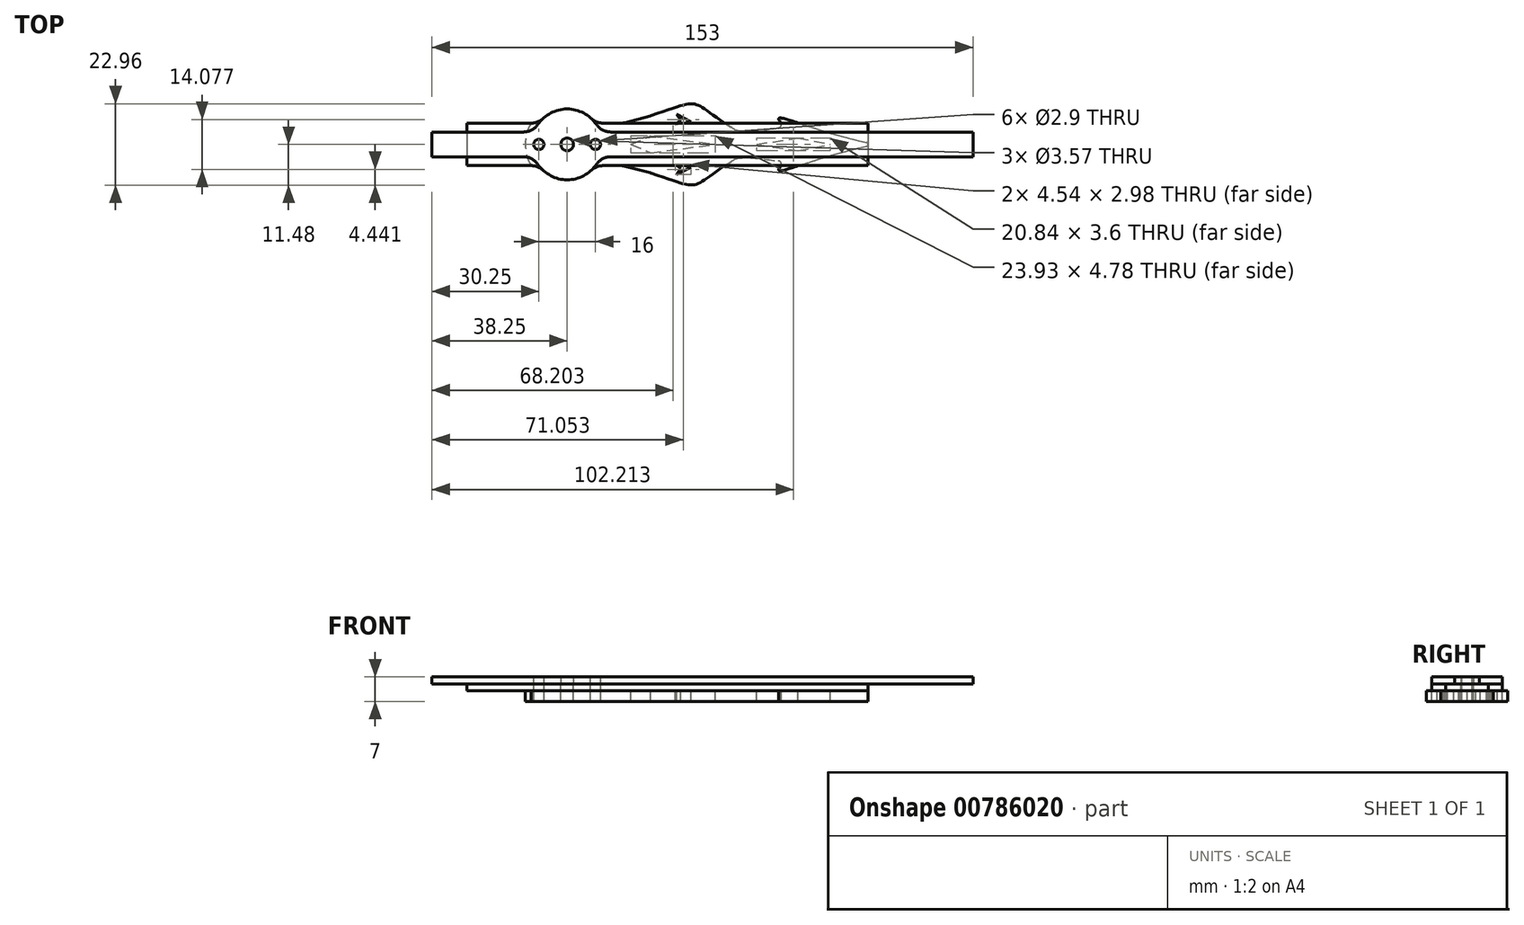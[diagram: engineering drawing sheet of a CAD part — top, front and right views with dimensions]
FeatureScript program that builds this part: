
annotation { "Feature Type Name" : "Feature", "Feature Type Description" : "" }
export const myFeature = defineFeature(function(context is Context, id is Id, definition is map)
    precondition{}
    {
        {
            var Q0;
            Q0=qCreatedBy(makeId("Top.planeOp"),FACE);
            var sketch = newSketch(context, id + "F0", { "sketchPlane" : qUnion([Q0])});
            skCircle(sketch, "E0", {"center": v(0, 0) * mm, "radius": 1.79 * mm});
            skLineSegment(sketch, "E1.bottom", {"start": v(-38.25, 3.5) * mm, "end": v(114.75, 3.5) * mm});
            skLineSegment(sketch, "E1.top", {"start": v(-38.25, -3.5) * mm, "end": v(114.75, -3.5) * mm});
            skLineSegment(sketch, "E1.left", {"start": v(-38.25, 3.5) * mm, "end": v(-38.25, -3.5) * mm});
            skLineSegment(sketch, "E1.right", {"start": v(114.75, 3.5) * mm, "end": v(114.75, -3.5) * mm});
            skCircle(sketch, "E2", {"center": v(0, 0) * mm, "radius": 10 * mm});
            skSolve(sketch);
        }
        {
            var Q0;
            Q0=qSketchRegion(id+"F0",true);
            extrude(context, id + "F1", {"entities" : qUnion([Q0]), "depth" : 2 * mm});
        }
        {
            var Q0;
            Q0=qCreatedBy(makeId("Top.planeOp"),FACE);
            var sketch = newSketch(context, id + "F2", { "sketchPlane" : qUnion([Q0])});
            skCircle(sketch, "E3", {"center": v(0, 0) * mm, "radius": 1.79 * mm});
            skLineSegment(sketch, "E4.bottom", {"start": v(-28.33, 6) * mm, "end": v(85, 6) * mm});
            skLineSegment(sketch, "E4.top", {"start": v(-28.33, -6) * mm, "end": v(85, -6) * mm});
            skLineSegment(sketch, "E4.left", {"start": v(-28.33, 6) * mm, "end": v(-28.33, -6) * mm});
            skLineSegment(sketch, "E4.right", {"start": v(85, 6) * mm, "end": v(85, -6) * mm});
            skCircle(sketch, "E5", {"center": v(0, 0) * mm, "radius": 10 * mm});
            skSolve(sketch);
        }
        {
            var Q0;
            Q0=qSketchRegion(id+"F2",true);
            extrude(context, id + "F3", {"entities" : qUnion([Q0]), "oppositeDirection" : true, "depth" : 2 * mm});
        }
        {
            var Q0;
            Q0=makeQuery(id+"F1.opExtrude","CAP_FACE",FACE,{"disambiguationData":[OSD([sQuery(id+"F0.wireOp",EDGE,"E0"),sQuery(id+"F0.wireOp",EDGE,"E1.bottom"),sQuery(id+"F0.wireOp",EDGE,"E1.top"),sQuery(id+"F0.wireOp",EDGE,"E1.left"),sQuery(id+"F0.wireOp",EDGE,"E1.right"),sQuery(id+"F0.wireOp",EDGE,"E2")])],"isStart":false});
            var sketch = newSketch(context, id + "F4", { "sketchPlane" : qUnion([Q0])});
            skCircle(sketch, "E6", {"center": v(8, 0) * mm, "radius": 1.45 * mm});
            skLineSegment(sketch, "E7", {"start": v(0, 0) * mm, "end": v(16, 0) * mm, "construction": true});
            skLineSegment(sketch, "E8", {"start": v(0, 0) * mm, "end": v(0, 19.04) * mm, "construction": true});
            skCircle(sketch, "E9.MirrorC", {"center": v(-8, 0) * mm, "radius": 1.45 * mm});
            skSolve(sketch);
        }
        {
            var Q0;
            Q0=qSketchRegion(id+"F4",true);
            extrude(context, id + "F5", {"entities" : qUnion([Q0]), "operationType" : NewBodyOperationType.REMOVE, "oppositeDirection" : true, "depth" : 25 * mm, "offsetDistance" : 25 * mm});
        }
        {
            var Q0;
            {var subQ0=sQuery(id+"F0.wireOp",EDGE,"E2");var subQ1=sQuery(id+"F0.wireOp",EDGE,"E1.top");Q0=makeQuery(id+"F1.opExtrude","SWEPT_EDGE",EDGE,{"disambiguationData":[OSD([subQ1,subQ0]),TDD([makeQuery(id+"F0.imprint","INTERSECT",VERTEX,{"disambiguationData":[OD(1.0)],"derivedFrom":[subQ1,subQ0]})])]});}
            var Q1;
            {var subQ0=sQuery(id+"F0.wireOp",EDGE,"E2");var subQ1=sQuery(id+"F0.wireOp",EDGE,"E1.bottom");Q1=makeQuery(id+"F1.opExtrude","SWEPT_EDGE",EDGE,{"disambiguationData":[OSD([subQ1,subQ0]),TDD([makeQuery(id+"F0.imprint","INTERSECT",VERTEX,{"disambiguationData":[OD(1.0)],"derivedFrom":[subQ1,subQ0]})])]});}
            var Q2;
            {var subQ0=sQuery(id+"F0.wireOp",EDGE,"E2");var subQ1=sQuery(id+"F0.wireOp",EDGE,"E1.bottom");Q2=makeQuery(id+"F1.opExtrude","SWEPT_EDGE",EDGE,{"disambiguationData":[OSD([subQ1,subQ0]),TDD([makeQuery(id+"F0.imprint","INTERSECT",VERTEX,{"disambiguationData":[OD(0.0)],"derivedFrom":[subQ1,subQ0]})])]});}
            var Q3;
            {var subQ0=sQuery(id+"F0.wireOp",EDGE,"E2");var subQ1=sQuery(id+"F0.wireOp",EDGE,"E1.top");Q3=makeQuery(id+"F1.opExtrude","SWEPT_EDGE",EDGE,{"disambiguationData":[OSD([subQ1,subQ0]),TDD([makeQuery(id+"F0.imprint","INTERSECT",VERTEX,{"disambiguationData":[OD(0.0)],"derivedFrom":[subQ1,subQ0]})])]});}
            var Q4;
            {var subQ0=sQuery(id+"F2.wireOp",EDGE,"E5");var subQ1=sQuery(id+"F2.wireOp",EDGE,"E4.top");Q4=makeQuery(id+"F3.opExtrude","SWEPT_EDGE",EDGE,{"disambiguationData":[OSD([subQ1,subQ0]),TDD([makeQuery(id+"F2.imprint","INTERSECT",VERTEX,{"disambiguationData":[OD(0.0)],"derivedFrom":[subQ1,subQ0]})])]});}
            var Q5;
            {var subQ0=sQuery(id+"F2.wireOp",EDGE,"E5");var subQ1=sQuery(id+"F2.wireOp",EDGE,"E4.bottom");Q5=makeQuery(id+"F3.opExtrude","SWEPT_EDGE",EDGE,{"disambiguationData":[OSD([subQ1,subQ0]),TDD([makeQuery(id+"F2.imprint","INTERSECT",VERTEX,{"disambiguationData":[OD(1.0)],"derivedFrom":[subQ1,subQ0]})])]});}
            var Q6;
            {var subQ0=sQuery(id+"F2.wireOp",EDGE,"E5");var subQ1=sQuery(id+"F2.wireOp",EDGE,"E4.top");Q6=makeQuery(id+"F3.opExtrude","SWEPT_EDGE",EDGE,{"disambiguationData":[OSD([subQ1,subQ0]),TDD([makeQuery(id+"F2.imprint","INTERSECT",VERTEX,{"disambiguationData":[OD(1.0)],"derivedFrom":[subQ1,subQ0]})])]});}
            var Q7;
            {var subQ0=sQuery(id+"F2.wireOp",EDGE,"E5");var subQ1=sQuery(id+"F2.wireOp",EDGE,"E4.bottom");Q7=makeQuery(id+"F3.opExtrude","SWEPT_EDGE",EDGE,{"disambiguationData":[OSD([subQ1,subQ0]),TDD([makeQuery(id+"F2.imprint","INTERSECT",VERTEX,{"disambiguationData":[OD(0.0)],"derivedFrom":[subQ1,subQ0]})])]});}
            fillet(context, id + "F6", {"entities" : qUnion([Q0, Q1, Q2, Q3, Q4, Q5, Q6, Q7]), "radius" : 5 * mm, "tangentPropagation" : true, "allowEdgeOverflow" : false});
        }
        {
            var Q0;
            Q0=makeQuery(id+"F3.opExtrude","CAP_FACE",FACE,{"disambiguationData":[OSD([sQuery(id+"F2.wireOp",EDGE,"E3"),sQuery(id+"F2.wireOp",EDGE,"E4.bottom"),sQuery(id+"F2.wireOp",EDGE,"E4.top"),sQuery(id+"F2.wireOp",EDGE,"E4.left"),sQuery(id+"F2.wireOp",EDGE,"E4.right"),sQuery(id+"F2.wireOp",EDGE,"E5")])],"isStart":false});
            var sketch = newSketch(context, id + "F7", { "sketchPlane" : qUnion([Q0])});
            skLineSegment(sketch, "E10", {"start": v(17.99, 0) * mm, "end": v(23.59, 2.39) * mm});
            skLineSegment(sketch, "E11", {"start": v(23.59, 2.39) * mm, "end": v(41.92, 0) * mm});
            skLineSegment(sketch, "E12", {"start": v(53.54, 0) * mm, "end": v(65.27, 1.8) * mm});
            skLineSegment(sketch, "E13", {"start": v(65.27, 1.8) * mm, "end": v(74.38, 0) * mm});
            skLineSegment(sketch, "E14", {"start": v(0, 0) * mm, "end": v(74.38, 0) * mm, "construction": true});
            skCircle(sketch, "E15", {"center": v(0, 0) * mm, "radius": 11.83 * mm});
            skLineSegment(sketch, "E16.bottom", {"start": v(-10.2, 6) * mm, "end": v(-28.33, 6) * mm});
            skLineSegment(sketch, "E16.top", {"start": v(-10.2, -6) * mm, "end": v(-28.33, -6) * mm});
            skLineSegment(sketch, "E16.left", {"start": v(-10.2, 6) * mm, "end": v(-10.2, -6) * mm});
            skLineSegment(sketch, "E16.right", {"start": v(-28.33, 6) * mm, "end": v(-28.33, -6) * mm});
            skCircle(sketch, "E17", {"center": v(0, 0) * mm, "radius": 1.79 * mm});
            skCircle(sketch, "E18", {"center": v(8, 0) * mm, "radius": 1.45 * mm});
            skCircle(sketch, "E19", {"center": v(-8, 0) * mm, "radius": 1.45 * mm});
            skLineSegment(sketch, "E20", {"start": v(15.74, 6) * mm, "end": v(23.59, 8.08) * mm});
            skLineSegment(sketch, "E21", {"start": v(23.59, 8.08) * mm, "end": v(46.56, 4.73) * mm, "construction": true});
            skLineSegment(sketch, "E22", {"start": v(46.56, 4.73) * mm, "end": v(61.74, 4.73) * mm});
            skLineSegment(sketch, "E23", {"start": v(61.74, 4.73) * mm, "end": v(65.27, 4.73) * mm});
            skLineSegment(sketch, "E24", {"start": v(68.44, 6) * mm, "end": v(86.86, 0) * mm});
            skLineSegment(sketch, "E25", {"start": v(15.74, 6) * mm, "end": v(10.2, 6) * mm});
            skLineSegment(sketch, "E26", {"start": v(11.83, 0) * mm, "end": v(17.99, 0) * mm});
            skLineSegment(sketch, "E27", {"start": v(41.92, 0) * mm, "end": v(53.54, 0) * mm});
            skLineSegment(sketch, "E28.MirrorCS", {"start": v(23.59, -2.39) * mm, "end": v(41.92, 0) * mm});
            skLineSegment(sketch, "E29.MirrorCS", {"start": v(17.99, 0) * mm, "end": v(23.59, -2.39) * mm});
            skLineSegment(sketch, "E30.MirrorCS", {"start": v(15.74, -6) * mm, "end": v(23.59, -8.08) * mm});
            skLineSegment(sketch, "E31.MirrorCS", {"start": v(23.59, -8.08) * mm, "end": v(46.56, -4.73) * mm, "construction": true});
            skLineSegment(sketch, "E32.MirrorCS", {"start": v(46.56, -4.73) * mm, "end": v(61.74, -4.73) * mm});
            skLineSegment(sketch, "E33.MirrorCS", {"start": v(61.74, -4.73) * mm, "end": v(65.27, -4.73) * mm, "construction": true});
            skLineSegment(sketch, "E34.MirrorCS", {"start": v(68.44, -6) * mm, "end": v(86.86, 0) * mm});
            skLineSegment(sketch, "E35.MirrorCS", {"start": v(53.54, 0) * mm, "end": v(65.27, -1.8) * mm});
            skLineSegment(sketch, "E36.MirrorCS", {"start": v(65.27, -1.8) * mm, "end": v(74.38, 0) * mm});
            skLineSegment(sketch, "E37.MirrorCS", {"start": v(15.74, -6) * mm, "end": v(10.2, -6) * mm});
            skLineSegment(sketch, "E38", {"start": v(23.59, 8.08) * mm, "end": v(23.59, -8.08) * mm, "construction": true});
            skLineSegment(sketch, "E39", {"start": v(65.27, 4.73) * mm, "end": v(65.27, -4.73) * mm, "construction": true});
            skFitSpline(sketch, "E40", {"points": [v(23.59, 8.08) * mm, v(46.56, 4.73) * mm], "startDerivative": vector(46.65, 15.55) * mm, "endDerivative": vector(38.51, -24.21) * mm});
            skFitSpline(sketch, "E41.MirrorCS", {"points": [v(23.59, -8.08) * mm, v(46.56, -4.73) * mm], "startDerivative": vector(46.65, -15.55) * mm, "endDerivative": vector(38.51, 24.21) * mm});
            skFitSpline(sketch, "E42", {"points": [v(61.74, 4.73) * mm, v(86.86, 0) * mm], "startDerivative": vector(-19.7, 19.46) * mm, "endDerivative": vector(64.75, -14.2) * mm});
            skFitSpline(sketch, "E43.MirrorCS", {"points": [v(61.74, -4.73) * mm, v(86.86, 0) * mm], "startDerivative": vector(-19.7, -19.46) * mm, "endDerivative": vector(64.75, 14.2) * mm});
            skLineSegment(sketch, "E44", {"start": v(30.97, 8.53) * mm, "end": v(32.11, 6.84) * mm});
            skLineSegment(sketch, "E45", {"start": v(30.97, 8.53) * mm, "end": v(35.07, 6.4) * mm});
            skLineSegment(sketch, "E46.MirrorCS", {"start": v(30.53, 5.55) * mm, "end": v(32.11, 6.84) * mm});
            skLineSegment(sketch, "E47.MirrorCS", {"start": v(30.53, 5.55) * mm, "end": v(35.07, 6.4) * mm});
            skLineSegment(sketch, "E48.MirrorCS", {"start": v(30.97, -8.53) * mm, "end": v(35.07, -6.4) * mm});
            skLineSegment(sketch, "E49.MirrorCS", {"start": v(30.97, -8.53) * mm, "end": v(32.11, -6.84) * mm});
            skLineSegment(sketch, "E50.MirrorCS", {"start": v(30.53, -5.55) * mm, "end": v(32.11, -6.84) * mm});
            skLineSegment(sketch, "E51.MirrorCS", {"start": v(30.53, -5.55) * mm, "end": v(35.07, -6.4) * mm});
            skLineSegment(sketch, "E52.MirrorCS", {"start": v(23.59, 8.08) * mm, "end": v(46.56, 4.73) * mm});
            skLineSegment(sketch, "E53.MirrorCS", {"start": v(61.74, 4.73) * mm, "end": v(65.27, 4.73) * mm, "construction": true});
            skPoint(sketch, "E54", {"position": v(85, 0) * mm});
            skFitSpline(sketch, "E55", {"points": [v(46.56, 4.73) * mm, v(61.74, 4.73) * mm], "startDerivative": vector(7.8, -6.9) * mm, "endDerivative": vector(15.18, 0) * mm});
            skFitSpline(sketch, "E56.MirrorCS", {"points": [v(46.56, -4.73) * mm, v(61.74, -4.73) * mm], "startDerivative": vector(7.8, 6.9) * mm, "endDerivative": vector(15.18, 0) * mm});
            skSolve(sketch);
        }
        {
            var Q0;
            {var subQ1=sQuery(id+"F2.wireOp",EDGE,"E5");var subQ2=sQuery(id+"F2.wireOp",EDGE,"E4.top");var subQ4=makeQuery(id+"F2.imprint","INTERSECT",VERTEX,{"disambiguationData":[OD(0.0)],"derivedFrom":[subQ2,subQ1]});Q0=makeQuery(id+"F7.imprint","IMPRINT",FACE,{"disambiguationData":[TD([[makeQuery(id+"F7.imprint","IMPRINT",EDGE,{"derivedFrom":makeQuery(id+"F3.opExtrude","CAP_EDGE",EDGE,{"disambiguationData":[OSD([subQ1]),TDD([makeQuery(id+"F2.imprint","IMPRINT",EDGE,{"disambiguationData":[TD([[subQ4,-1.0]])],"derivedFrom":subQ1})])],"isStart":false})}),1.0]])]});}
            var Q1;
            {var subQ1=sQuery(id+"F2.wireOp",EDGE,"E5");var subQ2=sQuery(id+"F2.wireOp",EDGE,"E4.bottom");var subQ4=makeQuery(id+"F2.imprint","INTERSECT",VERTEX,{"disambiguationData":[OD(0.0)],"derivedFrom":[subQ2,subQ1]});Q1=makeQuery(id+"F7.imprint","IMPRINT",FACE,{"disambiguationData":[TD([[makeQuery(id+"F7.imprint","IMPRINT",EDGE,{"derivedFrom":makeQuery(id+"F3.opExtrude","CAP_EDGE",EDGE,{"disambiguationData":[OSD([subQ1]),TDD([makeQuery(id+"F2.imprint","IMPRINT",EDGE,{"disambiguationData":[TD([[subQ4,1.0]])],"derivedFrom":subQ1})])],"isStart":false})}),1.0]])]});}
            var Q2;
            {var subQ0=sQuery(id+"F7.wireOp",EDGE,"E16.left");Q2=makeQuery(id+"F7.imprint","IMPRINT",FACE,{"disambiguationData":[TD([[makeQuery(id+"F7.imprint","IMPRINT",EDGE,{"derivedFrom":subQ0}),-1.0]])]});}
            var Q3;
            Q3=makeQuery(id+"F7.imprint","IMPRINT",FACE,{"disambiguationData":[TD([[makeQuery(id+"F7.imprint","IMPRINT",EDGE,{"derivedFrom":sQuery(id+"F7.wireOp",EDGE,"E16.left")}),1.0]])]});
            var Q4;
            {var subQ0=sQuery(id+"F7.wireOp",EDGE,"E20");Q4=makeQuery(id+"F7.imprint","IMPRINT",FACE,{"disambiguationData":[TD([[makeQuery(id+"F7.imprint","IMPRINT",EDGE,{"derivedFrom":subQ0}),-1.0]])]});}
            var Q5;
            {var subQ0=sQuery(id+"F7.wireOp",EDGE,"E30.MirrorCS");Q5=makeQuery(id+"F7.imprint","IMPRINT",FACE,{"disambiguationData":[TD([[makeQuery(id+"F7.imprint","IMPRINT",EDGE,{"derivedFrom":subQ0}),1.0]])]});}
            var Q6;
            Q6=makeQuery(id+"F7.imprint","IMPRINT",FACE,{"disambiguationData":[TD([[makeQuery(id+"F7.imprint","IMPRINT",EDGE,{"derivedFrom":sQuery(id+"F7.wireOp",EDGE,"E10")}),1.0]])]});
            var Q7;
            {var subQ12=sQuery(id+"F7.wireOp",EDGE,"E26");Q7=makeQuery(id+"F7.imprint","IMPRINT",FACE,{"disambiguationData":[TD([[makeQuery(id+"F7.imprint","IMPRINT",EDGE,{"derivedFrom":subQ12}),-1.0]])]});}
            var Q8;
            {var subQ0=sQuery(id+"F7.wireOp",EDGE,"E40");var subQ1=sQuery(id+"F7.wireOp",EDGE,"E21");var subQ2=makeQuery(id+"F7.imprint","INTERSECT",VERTEX,{"derivedFrom":[sQuery(id+"F7.wireOp",EDGE,"E20"),subQ1,subQ0]});Q8=makeQuery(id+"F7.imprint","IMPRINT",FACE,{"disambiguationData":[TD([[makeQuery(id+"F7.imprint","IMPRINT",EDGE,{"disambiguationData":[TD([[subQ2,-1.0]])],"derivedFrom":subQ1}),1.0]])]});}
            var Q9;
            {var subQ0=sQuery(id+"F7.wireOp",EDGE,"E41.MirrorCS");var subQ1=sQuery(id+"F7.wireOp",EDGE,"E31.MirrorCS");var subQ2=makeQuery(id+"F7.imprint","INTERSECT",VERTEX,{"derivedFrom":[sQuery(id+"F7.wireOp",EDGE,"E30.MirrorCS"),subQ1,subQ0]});Q9=makeQuery(id+"F7.imprint","IMPRINT",FACE,{"disambiguationData":[TD([[makeQuery(id+"F7.imprint","IMPRINT",EDGE,{"disambiguationData":[TD([[subQ2,-1.0]])],"derivedFrom":subQ1}),-1.0]])]});}
            var Q10;
            {var subQ0=sQuery(id+"F7.wireOp",EDGE,"E41.MirrorCS");var subQ1=sQuery(id+"F7.wireOp",EDGE,"E31.MirrorCS");var subQ2=makeQuery(id+"F7.imprint","INTERSECT",VERTEX,{"derivedFrom":[subQ1,sQuery(id+"F7.wireOp",EDGE,"E32.MirrorCS"),subQ0]});Q10=makeQuery(id+"F7.imprint","IMPRINT",FACE,{"disambiguationData":[TD([[makeQuery(id+"F7.imprint","IMPRINT",EDGE,{"disambiguationData":[TD([[subQ2,1.0]])],"derivedFrom":subQ1}),-1.0]])]});}
            var Q11;
            {var subQ0=sQuery(id+"F7.wireOp",EDGE,"E40");var subQ1=sQuery(id+"F7.wireOp",EDGE,"E21");var subQ2=makeQuery(id+"F7.imprint","INTERSECT",VERTEX,{"derivedFrom":[subQ1,sQuery(id+"F7.wireOp",EDGE,"E22"),subQ0]});Q11=makeQuery(id+"F7.imprint","IMPRINT",FACE,{"disambiguationData":[TD([[makeQuery(id+"F7.imprint","IMPRINT",EDGE,{"disambiguationData":[TD([[subQ2,1.0]])],"derivedFrom":subQ1}),1.0]])]});}
            var Q12;
            {var subQ0=sQuery(id+"F7.wireOp",EDGE,"E42");var subQ1=sQuery(id+"F2.wireOp",EDGE,"E4.top");var subQ2=makeQuery(id+"F3.opExtrude","CAP_EDGE",EDGE,{"disambiguationData":[OSD([subQ1]),TDD([makeQuery(id+"F2.imprint","IMPRINT",EDGE,{"disambiguationData":[TD([[makeQuery(id+"F2.imprint","INTERSECT",VERTEX,{"derivedFrom":[subQ1,sQuery(id+"F2.wireOp",EDGE,"E4.right")]}),1.0]])],"derivedFrom":subQ1})])],"isStart":false});var subQ3=makeQuery(id+"F7.imprint","INTERSECT",VERTEX,{"disambiguationData":[OD(0.0)],"derivedFrom":[subQ2,subQ0]});Q12=makeQuery(id+"F7.imprint","IMPRINT",FACE,{"disambiguationData":[TD([[makeQuery(id+"F7.imprint","IMPRINT",EDGE,{"disambiguationData":[TD([[subQ3,-1.0]])],"derivedFrom":subQ0}),-1.0]])]});}
            var Q13;
            {var subQ0=sQuery(id+"F7.wireOp",EDGE,"E23");Q13=makeQuery(id+"F7.imprint","IMPRINT",FACE,{"disambiguationData":[TD([[makeQuery(id+"F7.imprint","IMPRINT",EDGE,{"derivedFrom":subQ0}),1.0]])]});}
            var Q14;
            {var subQ1=sQuery(id+"F2.wireOp",EDGE,"E4.right");var subQ5=makeQuery(id+"F3.opExtrude","CAP_EDGE",EDGE,{"disambiguationData":[OSD([subQ1])],"isStart":false});var subQ7=sQuery(id+"F7.wireOp",EDGE,"E42");var subQ9=makeQuery(id+"F7.imprint","INTERSECT",VERTEX,{"derivedFrom":[subQ5,subQ7]});Q14=makeQuery(id+"F7.imprint","IMPRINT",FACE,{"disambiguationData":[TD([[makeQuery(id+"F7.imprint","IMPRINT",EDGE,{"disambiguationData":[TD([[subQ9,1.0]])],"derivedFrom":subQ5}),1.0]])]});}
            var Q15;
            {var subQ0=sQuery(id+"F7.wireOp",EDGE,"E42");var subQ1=sQuery(id+"F7.wireOp",EDGE,"E24");var subQ2=makeQuery(id+"F7.imprint","INTERSECT",VERTEX,{"derivedFrom":[subQ1,subQ0]});Q15=makeQuery(id+"F7.imprint","IMPRINT",FACE,{"disambiguationData":[TD([[makeQuery(id+"F7.imprint","IMPRINT",EDGE,{"disambiguationData":[TD([[subQ2,1.0]])],"derivedFrom":subQ1}),1.0]])]});}
            var Q16;
            {var subQ1=sQuery(id+"F2.wireOp",EDGE,"E4.right");var subQ5=makeQuery(id+"F3.opExtrude","CAP_EDGE",EDGE,{"disambiguationData":[OSD([subQ1])],"isStart":false});var subQ7=sQuery(id+"F7.wireOp",EDGE,"E43.MirrorCS");var subQ9=makeQuery(id+"F7.imprint","INTERSECT",VERTEX,{"derivedFrom":[subQ5,subQ7]});Q16=makeQuery(id+"F7.imprint","IMPRINT",FACE,{"disambiguationData":[TD([[makeQuery(id+"F7.imprint","IMPRINT",EDGE,{"disambiguationData":[TD([[subQ9,-1.0]])],"derivedFrom":subQ5}),1.0]])]});}
            var Q17;
            {var subQ0=sQuery(id+"F7.wireOp",EDGE,"E43.MirrorCS");var subQ1=sQuery(id+"F2.wireOp",EDGE,"E4.bottom");var subQ2=makeQuery(id+"F3.opExtrude","CAP_EDGE",EDGE,{"disambiguationData":[OSD([subQ1]),TDD([makeQuery(id+"F2.imprint","IMPRINT",EDGE,{"disambiguationData":[TD([[makeQuery(id+"F2.imprint","INTERSECT",VERTEX,{"derivedFrom":[subQ1,sQuery(id+"F2.wireOp",EDGE,"E4.right")]}),1.0]])],"derivedFrom":subQ1})])],"isStart":false});var subQ3=makeQuery(id+"F7.imprint","INTERSECT",VERTEX,{"disambiguationData":[OD(0.0)],"derivedFrom":[subQ2,subQ0]});Q17=makeQuery(id+"F7.imprint","IMPRINT",FACE,{"disambiguationData":[TD([[makeQuery(id+"F7.imprint","IMPRINT",EDGE,{"disambiguationData":[TD([[subQ3,-1.0]])],"derivedFrom":subQ0}),1.0]])]});}
            var Q18;
            {var subQ0=sQuery(id+"F7.wireOp",EDGE,"E33.MirrorCS");Q18=makeQuery(id+"F7.imprint","IMPRINT",FACE,{"disambiguationData":[TD([[makeQuery(id+"F7.imprint","IMPRINT",EDGE,{"derivedFrom":subQ0}),-1.0]])]});}
            var Q19;
            {var subQ0=sQuery(id+"F7.wireOp",EDGE,"E43.MirrorCS");var subQ1=sQuery(id+"F7.wireOp",EDGE,"E34.MirrorCS");var subQ2=makeQuery(id+"F7.imprint","INTERSECT",VERTEX,{"derivedFrom":[subQ1,subQ0]});Q19=makeQuery(id+"F7.imprint","IMPRINT",FACE,{"disambiguationData":[TD([[makeQuery(id+"F7.imprint","IMPRINT",EDGE,{"disambiguationData":[TD([[subQ2,1.0]])],"derivedFrom":subQ1}),-1.0]])]});}
            var Q20;
            {var subQ3=sQuery(id+"F7.wireOp",EDGE,"E46.MirrorCS");Q20=makeQuery(id+"F7.imprint","IMPRINT",FACE,{"disambiguationData":[TD([[makeQuery(id+"F7.imprint","IMPRINT",EDGE,{"derivedFrom":subQ3}),1.0]])]});}
            var Q21;
            {var subQ0=sQuery(id+"F7.wireOp",EDGE,"E52.MirrorCS");var subQ1=sQuery(id+"F7.wireOp",EDGE,"E40");var subQ2=makeQuery(id+"F7.imprint","INTERSECT",VERTEX,{"derivedFrom":[sQuery(id+"F7.wireOp",EDGE,"E22"),subQ1,subQ0]});Q21=makeQuery(id+"F7.imprint","IMPRINT",FACE,{"disambiguationData":[TD([[makeQuery(id+"F7.imprint","IMPRINT",EDGE,{"disambiguationData":[TD([[subQ2,1.0]])],"derivedFrom":subQ1}),-1.0]])]});}
            var Q22;
            {var subQ3=sQuery(id+"F7.wireOp",EDGE,"E44");Q22=makeQuery(id+"F7.imprint","IMPRINT",FACE,{"disambiguationData":[TD([[makeQuery(id+"F7.imprint","IMPRINT",EDGE,{"derivedFrom":subQ3}),-1.0]])]});}
            var Q23;
            {var subQ0=sQuery(id+"F7.wireOp",EDGE,"E52.MirrorCS");var subQ1=sQuery(id+"F7.wireOp",EDGE,"E47.MirrorCS");var subQ2=makeQuery(id+"F7.imprint","INTERSECT",VERTEX,{"derivedFrom":[sQuery(id+"F7.wireOp",EDGE,"E45"),subQ1,subQ0]});Q23=makeQuery(id+"F7.imprint","IMPRINT",FACE,{"disambiguationData":[TD([[makeQuery(id+"F7.imprint","IMPRINT",EDGE,{"disambiguationData":[TD([[subQ2,1.0]])],"derivedFrom":subQ1}),-1.0]])]});}
            var Q24;
            {var subQ1=sQuery(id+"F7.wireOp",EDGE,"E42");var subQ3=makeQuery(id+"F3.opExtrude","CAP_EDGE",EDGE,{"disambiguationData":[OSD([sQuery(id+"F2.wireOp",EDGE,"E4.right")])],"isStart":false});var subQ4=makeQuery(id+"F7.imprint","INTERSECT",VERTEX,{"derivedFrom":[subQ3,subQ1]});Q24=makeQuery(id+"F7.imprint","IMPRINT",FACE,{"disambiguationData":[TD([[makeQuery(id+"F7.imprint","IMPRINT",EDGE,{"disambiguationData":[TD([[subQ4,1.0]])],"derivedFrom":subQ3}),-1.0]])]});}
            extrude(context, id + "F8", {"entities" : qUnion([Q0, Q1, Q2, Q3, Q4, Q5, Q6, Q7, Q8, Q9, Q10, Q11, Q12, Q13, Q14, Q15, Q16, Q17, Q18, Q19, Q20, Q21, Q22, Q23, Q24]), "depth" : 3 * mm, "offsetDistance" : 25 * mm});
        }
        {
            var Q0;
            Q0=makeQuery(id+"F8.opExtrude","SWEPT_EDGE",EDGE,{"disambiguationData":[OSD([sQuery(id+"F7.wireOp",EDGE,"E22"),sQuery(id+"F7.wireOp",EDGE,"E40"),sQuery(id+"F7.wireOp",EDGE,"E52.MirrorCS")])]});
            var Q1;
            Q1=makeQuery(id+"F8.opExtrude","SWEPT_EDGE",EDGE,{"disambiguationData":[OSD([sQuery(id+"F2.wireOp",EDGE,"E4.top"),sQuery(id+"F7.wireOp",EDGE,"E20"),sQuery(id+"F7.wireOp",EDGE,"E25")])]});
            var Q2;
            Q2=makeQuery(id+"F8.opExtrude","SWEPT_EDGE",EDGE,{"disambiguationData":[OSD([sQuery(id+"F2.wireOp",EDGE,"E3"),sQuery(id+"F2.wireOp",EDGE,"E4.bottom"),sQuery(id+"F2.wireOp",EDGE,"E4.top"),sQuery(id+"F2.wireOp",EDGE,"E4.left"),sQuery(id+"F2.wireOp",EDGE,"E4.right"),sQuery(id+"F2.wireOp",EDGE,"E5"),sQuery(id+"F7.wireOp",EDGE,"E15"),sQuery(id+"F7.wireOp",EDGE,"E37.MirrorCS")])]});
            var Q3;
            Q3=makeQuery(id+"F8.opExtrude","SWEPT_EDGE",EDGE,{"disambiguationData":[OSD([sQuery(id+"F2.wireOp",EDGE,"E4.bottom"),sQuery(id+"F7.wireOp",EDGE,"E30.MirrorCS"),sQuery(id+"F7.wireOp",EDGE,"E37.MirrorCS")])]});
            var Q4;
            Q4=makeQuery(id+"F8.opExtrude","SWEPT_EDGE",EDGE,{"disambiguationData":[OSD([sQuery(id+"F2.wireOp",EDGE,"E3"),sQuery(id+"F2.wireOp",EDGE,"E4.bottom"),sQuery(id+"F2.wireOp",EDGE,"E4.top"),sQuery(id+"F2.wireOp",EDGE,"E4.left"),sQuery(id+"F2.wireOp",EDGE,"E4.right"),sQuery(id+"F2.wireOp",EDGE,"E5"),sQuery(id+"F7.wireOp",EDGE,"E15"),sQuery(id+"F7.wireOp",EDGE,"E25")])]});
            var Q5;
            Q5=makeQuery(id+"F8.opExtrude","SWEPT_EDGE",EDGE,{"disambiguationData":[OSD([sQuery(id+"F7.wireOp",EDGE,"E20"),sQuery(id+"F7.wireOp",EDGE,"E40"),sQuery(id+"F7.wireOp",EDGE,"E52.MirrorCS")])]});
            var Q6;
            Q6=makeQuery(id+"F8.opExtrude","SWEPT_EDGE",EDGE,{"disambiguationData":[OSD([sQuery(id+"F7.wireOp",EDGE,"E30.MirrorCS"),sQuery(id+"F7.wireOp",EDGE,"E41.MirrorCS")])]});
            var Q7;
            Q7=makeQuery(id+"F8.opExtrude","SWEPT_EDGE",EDGE,{"disambiguationData":[OSD([sQuery(id+"F7.wireOp",EDGE,"E32.MirrorCS"),sQuery(id+"F7.wireOp",EDGE,"E41.MirrorCS")])]});
            fillet(context, id + "F9", {"entities" : qUnion([Q0, Q1, Q2, Q3, Q4, Q5, Q6, Q7]), "radius" : 5 * mm, "tangentPropagation" : true, "allowEdgeOverflow" : false});
        }
        {
            var Q0;
            Q0=makeQuery(id+"F8.opExtrude","SWEPT_EDGE",EDGE,{"disambiguationData":[OSD([sQuery(id+"F7.wireOp",EDGE,"E22"),sQuery(id+"F7.wireOp",EDGE,"E42")])]});
            var Q1;
            Q1=makeQuery(id+"F8.opExtrude","SWEPT_EDGE",EDGE,{"disambiguationData":[OSD([sQuery(id+"F7.wireOp",EDGE,"E32.MirrorCS"),sQuery(id+"F7.wireOp",EDGE,"E43.MirrorCS")])]});
            fillet(context, id + "F10", {"entities" : qUnion([Q0, Q1]), "radius" : 1 * mm, "tangentPropagation" : true, "allowEdgeOverflow" : false});
        }
        {
            var Q0;
            Q0=makeQuery(id+"F8.opExtrude","SWEPT_EDGE",EDGE,{"disambiguationData":[OSD([sQuery(id+"F7.wireOp",EDGE,"E24"),sQuery(id+"F7.wireOp",EDGE,"E34.MirrorCS"),sQuery(id+"F7.wireOp",EDGE,"E42"),sQuery(id+"F7.wireOp",EDGE,"E43.MirrorCS")])]});
            fillet(context, id + "F11", {"entities" : qUnion([Q0]), "radius" : 0.5 * mm, "tangentPropagation" : true, "allowEdgeOverflow" : false});
        }
    });
